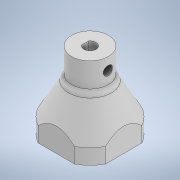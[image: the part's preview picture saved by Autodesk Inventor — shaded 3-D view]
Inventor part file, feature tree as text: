
AUTODESK INVENTOR PART (.ipt)
format: ipt  version: 2021 (Build 250183000, 183)  size: 208,384 bytes
history: native  units: mm
features: sketch x9, extrude x7, thread x3, other x2, loft x1, fillet x1
ambient origin geometry x8: Origin, YZ Plane, XZ Plane, XY Plane, X Axis, Y Axis, Z Axis, Center Point
bodies: Body1 (feature_tree)
feature tree (23):
  other  "Bryła1"
  extrude  "Wyciągnięcie proste1"  Depth=12.0mm
  extrude  "Wyciągnięcie proste2"  Depth=12.0mm
  thread  "Gwint1"
  extrude  "Wyciągnięcie proste3"  Depth=8.0mm TaperAngle=0.0deg
  extrude  "Wyciągnięcie proste4"  Depth=4.0mm
  loft  "Wyciągnięcie złożone2"
  sketch  "Szkic19"
  sketch  "Szkic20"
  extrude  "Wyciągnięcie proste6"  TaperAngle=0.0deg  [1 undecoded]
  extrude  "Wyciągnięcie proste7"  Depth=12.0mm TaperAngle=0.0deg
  extrude  "Wyciągnięcie proste8"  Depth=8.0mm TaperAngle=0.0deg
  thread  "Gwint2"
  thread  "Gwint3"
  fillet  "Zaokrąglenie1"  Radius=14.0mm
  sketch  "Szkic2"
  sketch  "Szkic5"
  sketch  "Szkic6"
  sketch  "Szkic11"
  sketch  "Szkic18"
  other  "Krawędzie2"
  sketch  "Szkic21"
  sketch  "Szkic22"
note: 1 required parameter value undecoded (feature->parameter linkage not recoverable at this tier; creation-order binding heuristic only, values carry confidence <= 0.55)
